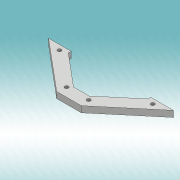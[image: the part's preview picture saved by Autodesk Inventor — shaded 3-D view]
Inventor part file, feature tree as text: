
AUTODESK INVENTOR PART (.ipt)
format: ipt  version: 2019 (Build 230136000, 136)  size: 118,272 bytes
history: native  units: mm
features: extrude x1, sketch x1
ambient origin geometry x8: Origin, YZ Plane, XZ Plane, XY Plane, X Axis, Y Axis, Z Axis, Center Point
bodies: Solid1 (feature_tree)
feature tree (2):
  extrude  "Extrusion1"  Depth=20.5mm
  sketch  "Sketch1"  dims[d6=6.0mm d8=6.981317mm d9=11.0mm d10=6.0mm d12=1.778mm d15=2.4mm d16=3.3mm d17=2.4mm d18=4.2mm d19=3.0mm d20=0.0mm d21=6.0mm d22=20.5mm]
